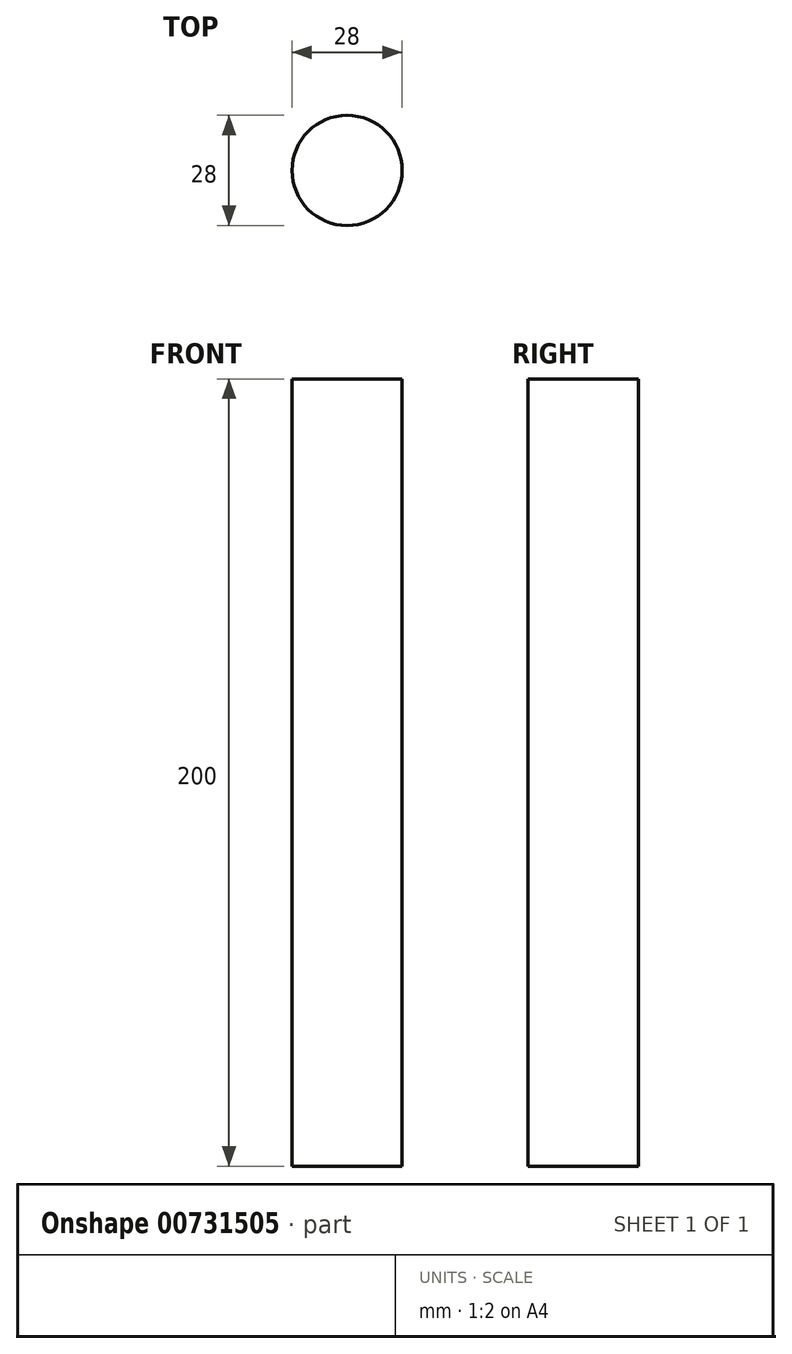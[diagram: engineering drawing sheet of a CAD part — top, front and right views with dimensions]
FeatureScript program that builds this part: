
annotation { "Feature Type Name" : "Feature", "Feature Type Description" : "" }
export const myFeature = defineFeature(function(context is Context, id is Id, definition is map)
    precondition{}
    {
        {
            var Q0;
            Q0=qCreatedBy(makeId("Top.planeOp"),FACE);
            var sketch = newSketch(context, id + "F0", { "sketchPlane" : qUnion([Q0])});
            skCircle(sketch, "E0", {"center": v(0, 0) * mm, "radius": 14 * mm});
            skSolve(sketch);
        }
        {
            var Q0;
            Q0 = qSketchRegion(id + "F0", true);
            extrude(context, id + "F1", {"entities" : qUnion([Q0]), "depth" : 200 * mm, "offsetDistance" : 25 * mm});
        }
    });
